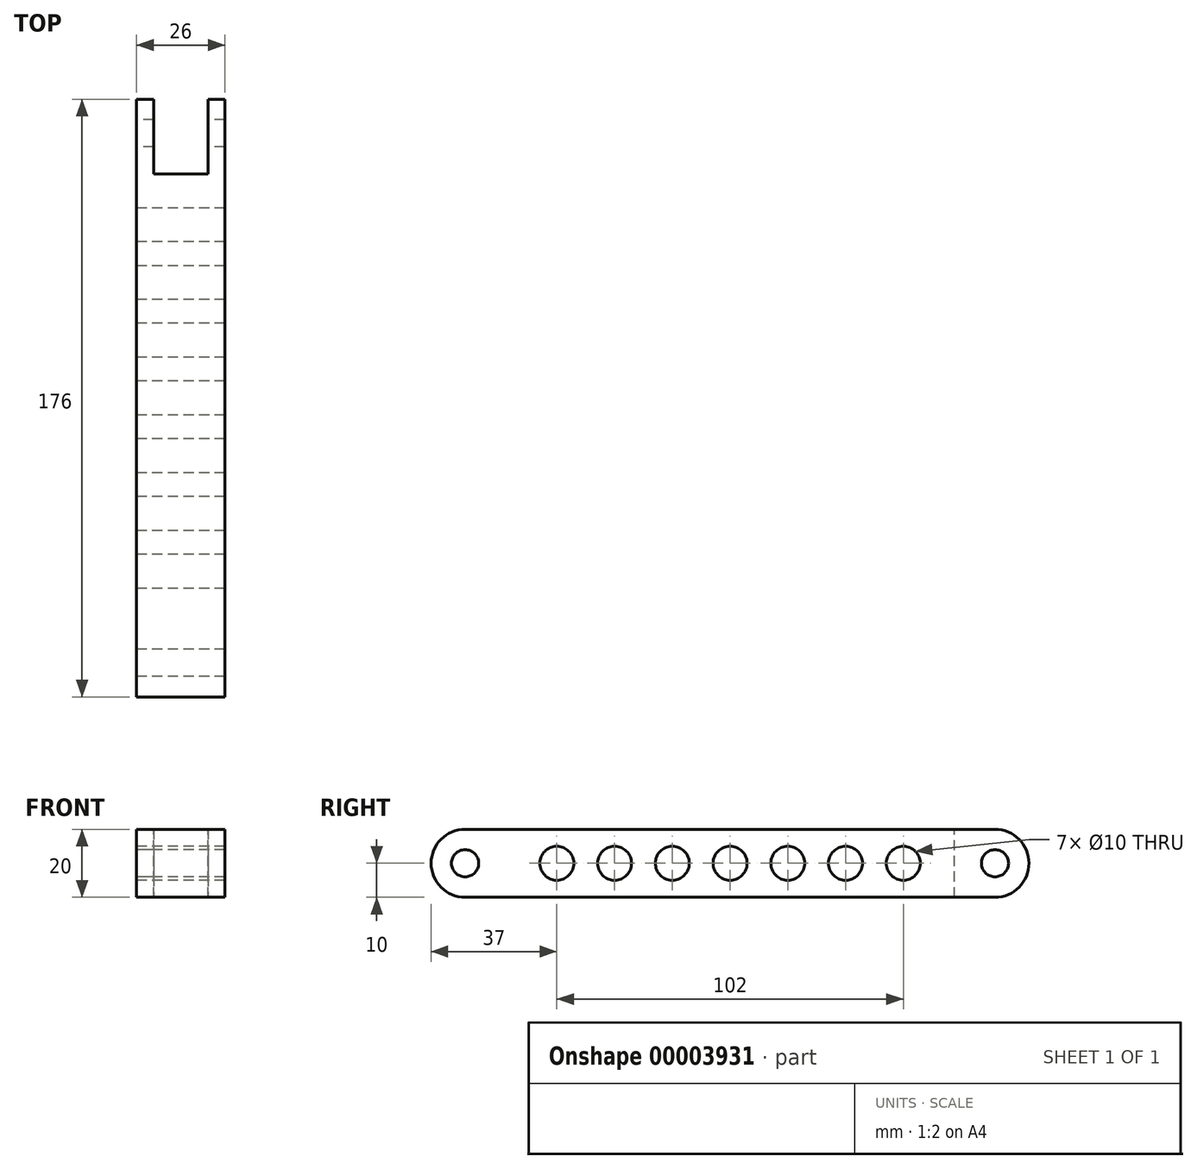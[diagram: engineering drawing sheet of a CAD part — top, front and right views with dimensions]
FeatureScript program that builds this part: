
annotation { "Feature Type Name" : "Feature", "Feature Type Description" : "" }
export const myFeature = defineFeature(function(context is Context, id is Id, definition is map)
    precondition{}
    {
        {
            var Q0;
            Q0=qCreatedBy(makeId("Right.planeOp"),FACE);
            var sketch = newSketch(context, id + "F0", { "sketchPlane" : qUnion([Q0])});
            skCircle(sketch, "E0", {"center": v(0, 0) * mm, "radius": 4 * mm});
            skCircle(sketch, "E1", {"center": v(0, 0) * mm, "radius": 10 * mm});
            skCircle(sketch, "E2", {"center": v(156, 0) * mm, "radius": 4 * mm});
            skCircle(sketch, "E3", {"center": v(156, 0) * mm, "radius": 10 * mm});
            skLineSegment(sketch, "E4", {"start": v(0, 10) * mm, "end": v(156, 10) * mm});
            skLineSegment(sketch, "E5", {"start": v(0, -10) * mm, "end": v(156, -10) * mm});
            skCircle(sketch, "E6", {"center": v(78, 0) * mm, "radius": 5 * mm});
            skLineSegment(sketch, "E7", {"start": v(0, 0) * mm, "end": v(156, 0) * mm, "construction": true});
            skCircle(sketch, "E8", {"center": v(95, 0) * mm, "radius": 5 * mm});
            skCircle(sketch, "E9", {"center": v(112, 0) * mm, "radius": 5 * mm});
            skCircle(sketch, "E10", {"center": v(129, 0) * mm, "radius": 5 * mm});
            skLineSegment(sketch, "E11", {"start": v(78, 0) * mm, "end": v(78, 38.81) * mm, "construction": true});
            skPoint(sketch, "E11.endSnap0", {"position": v(78, 10) * mm});
            skCircle(sketch, "E12.MirrorC", {"center": v(61, 0) * mm, "radius": 5 * mm});
            skCircle(sketch, "E13.MirrorC", {"center": v(44, 0) * mm, "radius": 5 * mm});
            skCircle(sketch, "E14.MirrorC", {"center": v(27, 0) * mm, "radius": 5 * mm});
            skSolve(sketch);
        }
        {
            var Q0;
            {var subQ1=sQuery(id+"F0.wireOp",EDGE,"E4");Q0=makeQuery(id+"F0.imprint","IMPRINT",FACE,{"disambiguationData":[TD([[makeQuery(id+"F0.imprint","IMPRINT",EDGE,{"derivedFrom":subQ1}),-1.0]])]});}
            var Q1;
            Q1=makeQuery(id+"F0.imprint","IMPRINT",FACE,{"disambiguationData":[TD([[makeQuery(id+"F0.imprint","IMPRINT",EDGE,{"derivedFrom":sQuery(id+"F0.wireOp",EDGE,"E0")}),-1.0]])]});
            var Q2;
            Q2=makeQuery(id+"F0.imprint","IMPRINT",FACE,{"disambiguationData":[TD([[makeQuery(id+"F0.imprint","IMPRINT",EDGE,{"derivedFrom":sQuery(id+"F0.wireOp",EDGE,"E2")}),-1.0]])]});
            extrude(context, id + "F1", {"entities" : qUnion([Q0, Q1, Q2]), "endBound" : BoundingType.SYMMETRIC, "depth" : 26 * mm});
        }
        {
            var Q0;
            Q0=qCreatedBy(makeId("Top.planeOp"),FACE);
            var sketch = newSketch(context, id + "F2", { "sketchPlane" : qUnion([Q0])});
            skLineSegment(sketch, "E15", {"start": v(13, -10) * mm, "end": v(-13, -10) * mm});
            skLineSegment(sketch, "E16", {"start": v(0, -10) * mm, "end": v(-8, -10) * mm});
            skLineSegment(sketch, "E17", {"start": v(-8, -10) * mm, "end": v(-8, 12) * mm});
            skLineSegment(sketch, "E18", {"start": v(-8, 12) * mm, "end": v(8, 12) * mm});
            skLineSegment(sketch, "E19", {"start": v(8, 12) * mm, "end": v(8, -10) * mm});
            skLineSegment(sketch, "E20", {"start": v(8, -10) * mm, "end": v(0, -10) * mm});
            skLineSegment(sketch, "E21", {"start": v(-13, 166) * mm, "end": v(13, 166) * mm});
            skLineSegment(sketch, "E22", {"start": v(-8, 166) * mm, "end": v(-8, 144) * mm});
            skLineSegment(sketch, "E23", {"start": v(8, 166) * mm, "end": v(8, 144) * mm});
            skLineSegment(sketch, "E24", {"start": v(8, 144) * mm, "end": v(-8, 144) * mm});
            skSolve(sketch);
        }
        {
            var Q0;
            {var subQ0=sQuery(id+"F2.wireOp",EDGE,"E22");Q0=makeQuery(id+"F2.imprint","IMPRINT",FACE,{"disambiguationData":[TD([[makeQuery(id+"F2.imprint","IMPRINT",EDGE,{"derivedFrom":subQ0}),1.0]])]});}
            var Q1;
            Q1=makeQuery(id+"F2.imprint","IMPRINT",FACE,{"disambiguationData":[TD([[makeQuery(id+"F2.imprint","IMPRINT",EDGE,{"derivedFrom":sQuery(id+"F2.wireOp",EDGE,"E16")}),-1.0]])]});
            extrude(context, id + "F3", {"entities" : qUnion([Q0, Q1]), "operationType" : NewBodyOperationType.REMOVE, "endBound" : BoundingType.SYMMETRIC, "oppositeDirection" : true, "depth" : 25 * mm});
        }
    });
